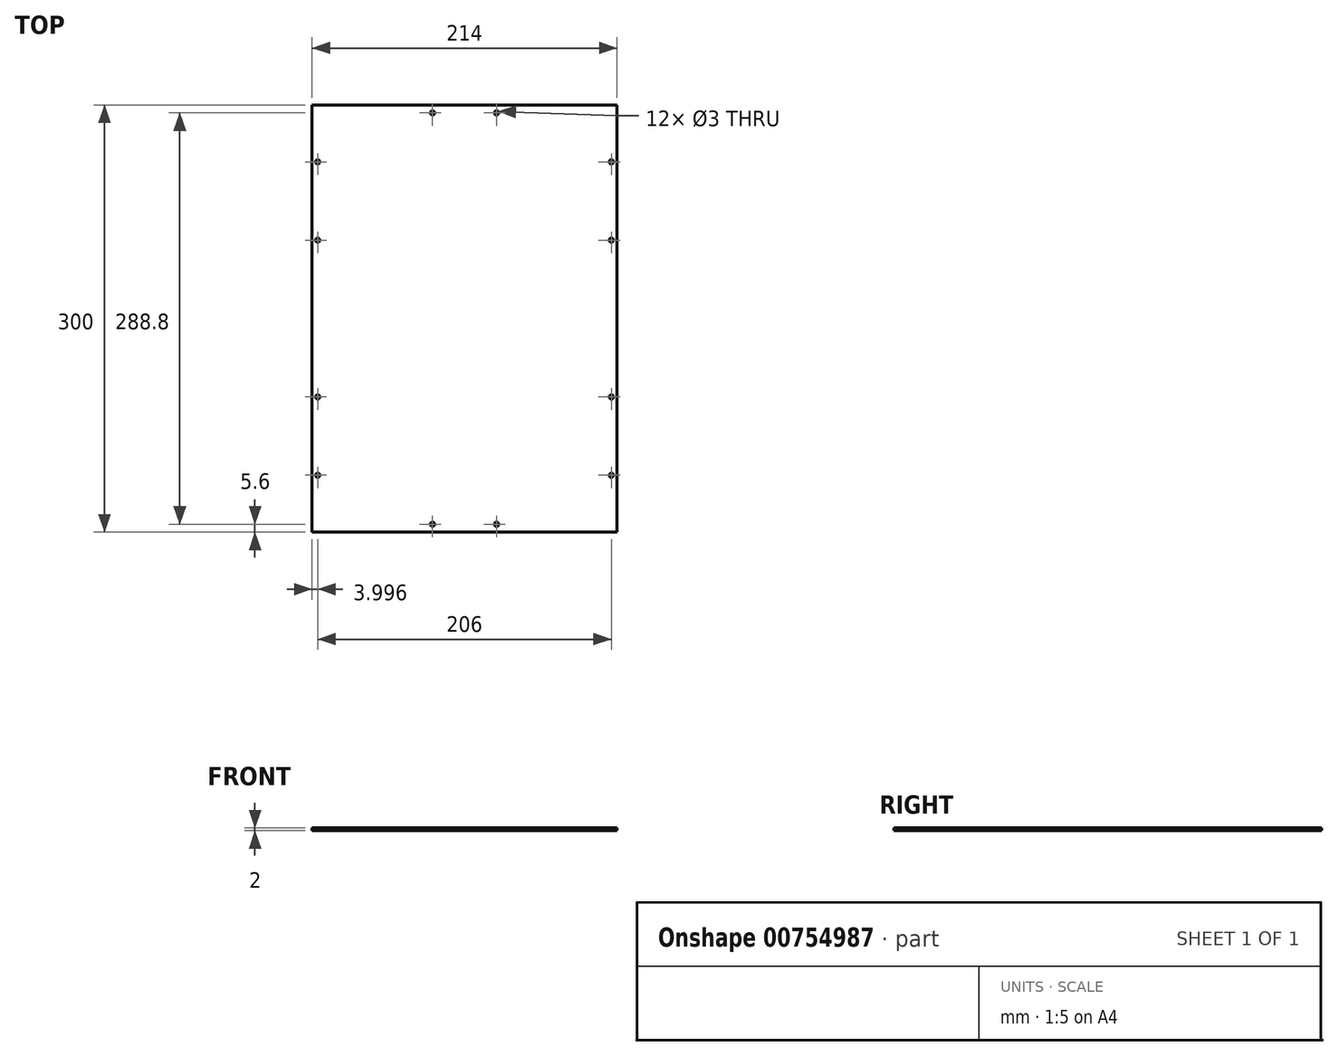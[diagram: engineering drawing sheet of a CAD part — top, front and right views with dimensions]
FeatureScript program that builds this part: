
annotation { "Feature Type Name" : "Feature", "Feature Type Description" : "" }
export const myFeature = defineFeature(function(context is Context, id is Id, definition is map)
    precondition{}
    {
        {
            var Q0;
            Q0=qCreatedBy(makeId("Top.planeOp"),FACE);
            var sketch = newSketch(context, id + "F0", { "sketchPlane" : qUnion([Q0])});
            skLineSegment(sketch, "E0.bottom", {"start": v(-119.42, 202.3) * mm, "end": v(94.58, 202.3) * mm});
            skLineSegment(sketch, "E0.top", {"start": v(-119.42, -97.7) * mm, "end": v(94.58, -97.7) * mm});
            skLineSegment(sketch, "E0.left", {"start": v(-119.42, 202.3) * mm, "end": v(-119.42, -97.7) * mm});
            skLineSegment(sketch, "E0.right", {"start": v(94.58, 202.3) * mm, "end": v(94.58, -97.7) * mm});
            skSolve(sketch);
        }
        {
            var Q0;
            Q0 = qSketchRegion(id + "F0", true);
            extrude(context, id + "F1", {"entities" : qUnion([Q0]), "depth" : 2 * mm, "offsetDistance" : 25 * mm});
        }
        {
            var Q0;
            Q0=makeQuery(id+"F1.opExtrude","CAP_FACE",FACE,{"disambiguationData":[OSD([sQuery(id+"F0.wireOp",EDGE,"E0.bottom"),sQuery(id+"F0.wireOp",EDGE,"E0.top"),sQuery(id+"F0.wireOp",EDGE,"E0.left"),sQuery(id+"F0.wireOp",EDGE,"E0.right")])],"isStart":false});
            var sketch = newSketch(context, id + "F2", { "sketchPlane" : qUnion([Q0])});
            skCircle(sketch, "E1", {"center": v(-115.42, -57.7) * mm, "radius": 1.5 * mm});
            skCircle(sketch, "E2", {"center": v(-115.42, -2.7) * mm, "radius": 1.5 * mm});
            skCircle(sketch, "E3", {"center": v(-115.42, 107.3) * mm, "radius": 1.5 * mm});
            skCircle(sketch, "E4", {"center": v(-115.42, 162.3) * mm, "radius": 1.5 * mm});
            skCircle(sketch, "E5", {"center": v(-34.92, 196.7) * mm, "radius": 1.5 * mm});
            skCircle(sketch, "E6", {"center": v(10.08, 196.7) * mm, "radius": 1.5 * mm});
            skCircle(sketch, "E7", {"center": v(90.58, 162.3) * mm, "radius": 1.5 * mm});
            skCircle(sketch, "E8", {"center": v(90.58, 107.3) * mm, "radius": 1.5 * mm});
            skCircle(sketch, "E9", {"center": v(90.58, -2.7) * mm, "radius": 1.5 * mm});
            skCircle(sketch, "E10", {"center": v(90.58, -57.7) * mm, "radius": 1.5 * mm});
            skCircle(sketch, "E11", {"center": v(-34.92, -92.1) * mm, "radius": 1.5 * mm});
            skCircle(sketch, "E12", {"center": v(10.08, -92.1) * mm, "radius": 1.5 * mm});
            skSolve(sketch);
        }
        {
            var Q0;
            Q0 = qSketchRegion(id + "F2", true);
            extrude(context, id + "F3", {"entities" : qUnion([Q0]), "operationType" : NewBodyOperationType.REMOVE, "oppositeDirection" : true, "depth" : 25 * mm, "offsetDistance" : 25 * mm});
        }
    });
